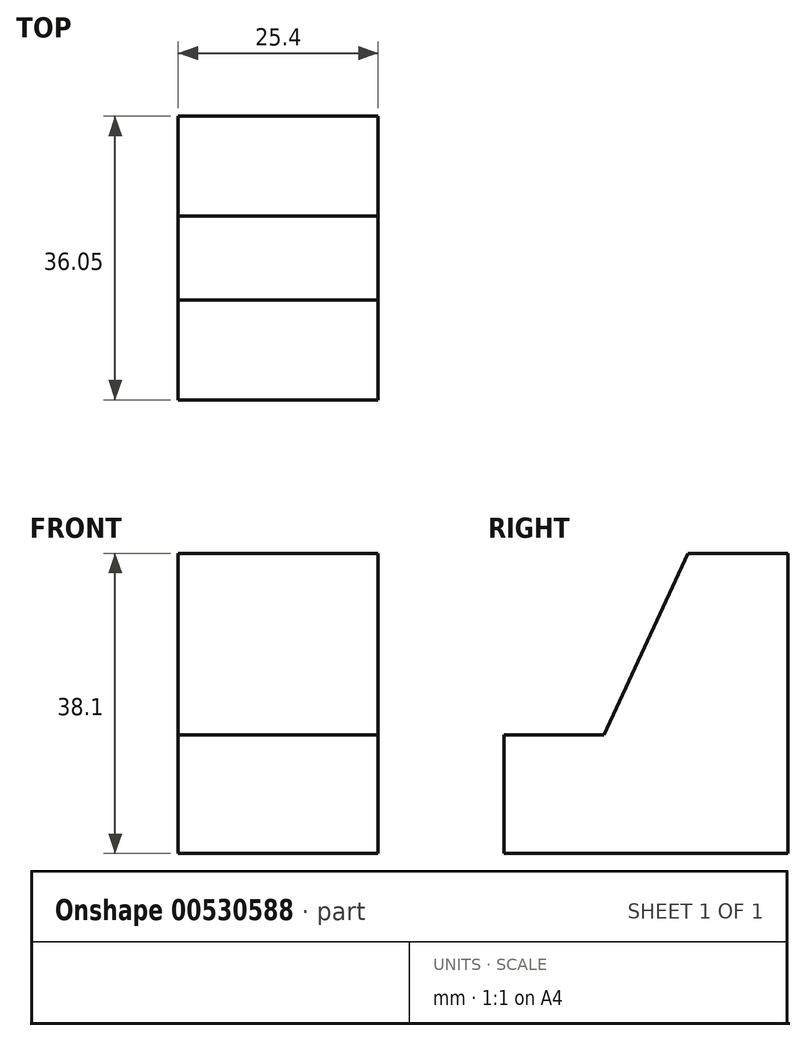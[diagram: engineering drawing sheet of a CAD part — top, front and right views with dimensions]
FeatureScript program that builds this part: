
annotation { "Feature Type Name" : "Feature", "Feature Type Description" : "" }
export const myFeature = defineFeature(function(context is Context, id is Id, definition is map)
    precondition{}
    {
        {
            var Q0;
            Q0=qCreatedBy(makeId("Right.planeOp"),FACE);
            var sketch = newSketch(context, id + "F0", { "sketchPlane" : qUnion([Q0])});
            skLineSegment(sketch, "E0", {"start": v(51.72, 39.65) * mm, "end": v(39.02, 39.65) * mm});
            skLineSegment(sketch, "E1", {"start": v(39.02, 39.65) * mm, "end": v(28.37, 16.59) * mm});
            skLineSegment(sketch, "E2", {"start": v(28.37, 16.59) * mm, "end": v(15.67, 16.59) * mm});
            skLineSegment(sketch, "E3", {"start": v(15.67, 16.59) * mm, "end": v(15.67, 1.55) * mm});
            skLineSegment(sketch, "E4", {"start": v(15.67, 1.55) * mm, "end": v(51.72, 1.55) * mm});
            skLineSegment(sketch, "E5", {"start": v(51.72, 1.55) * mm, "end": v(51.72, 39.65) * mm});
            skSolve(sketch);
        }
        {
            var Q0;
            Q0=makeQuery(id+"F0.imprint","IMPRINT",FACE,{"disambiguationData":[TD([[makeQuery(id+"F0.imprint","IMPRINT",EDGE,{"derivedFrom":sQuery(id+"F0.wireOp",EDGE,"E0")}),1.0]])]});
            extrude(context, id + "F1", {"entities" : qUnion([Q0]), "depth" : 25.4 * mm, "offsetDistance" : 25.4 * mm});
        }
    });
